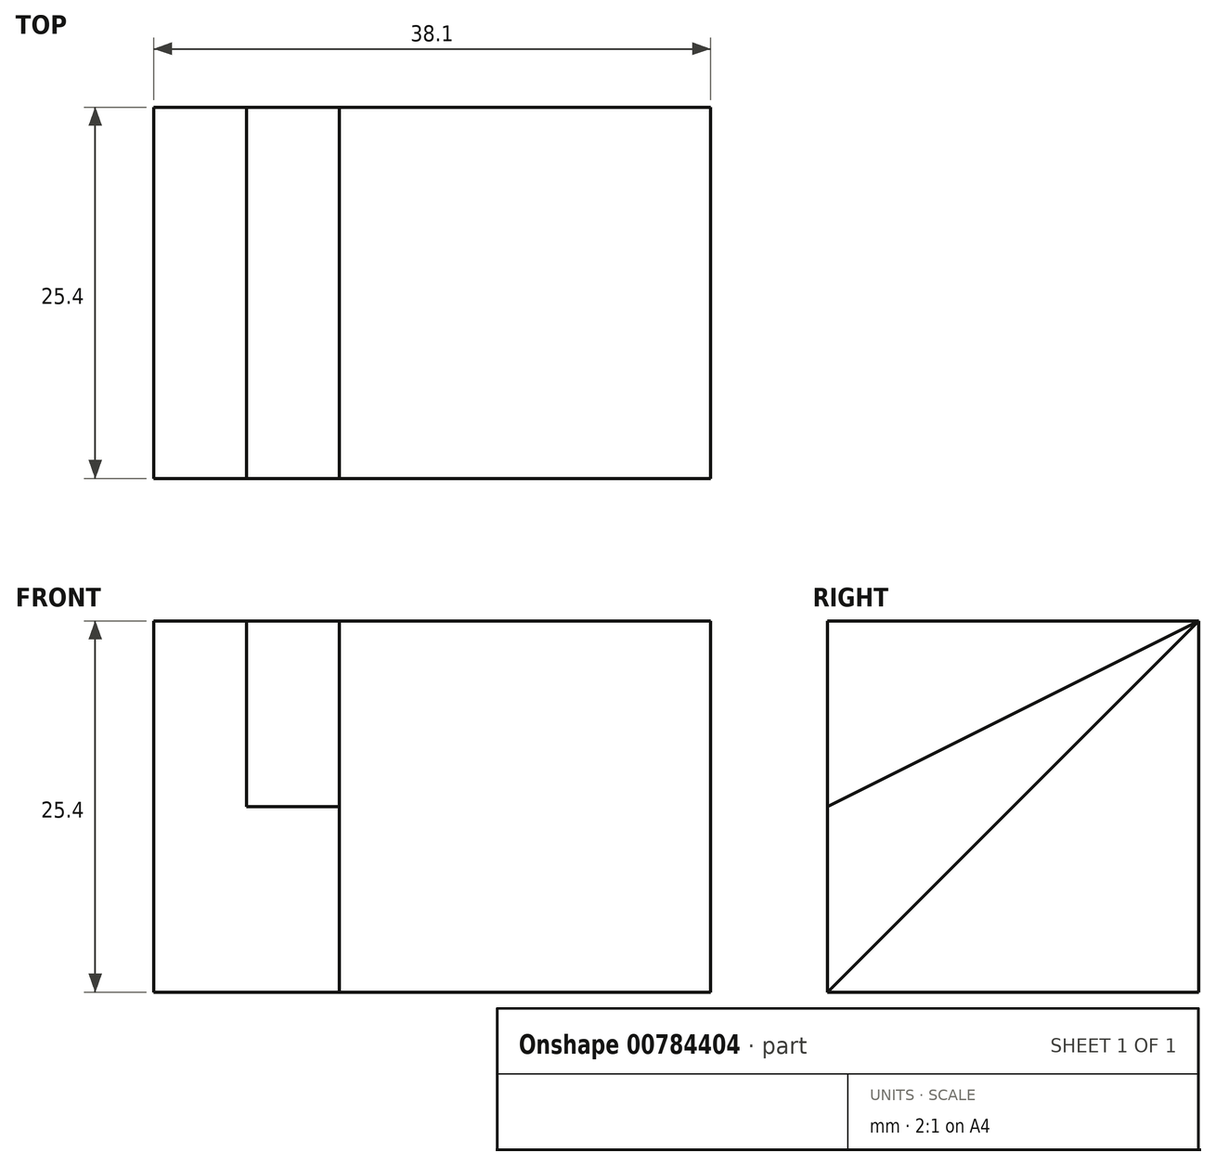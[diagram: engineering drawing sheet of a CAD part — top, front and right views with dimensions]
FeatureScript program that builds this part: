
annotation { "Feature Type Name" : "Feature", "Feature Type Description" : "" }
export const myFeature = defineFeature(function(context is Context, id is Id, definition is map)
    precondition{}
    {
        {
            var Q0;
            Q0=qCreatedBy(makeId("Front.planeOp"),FACE);
            var sketch = newSketch(context, id + "F0", { "sketchPlane" : qUnion([Q0])});
            skLineSegment(sketch, "E0", {"start": v(0, 0) * mm, "end": v(38.1, 0) * mm});
            skLineSegment(sketch, "E1", {"start": v(38.1, 0) * mm, "end": v(38.1, 25.4) * mm});
            skLineSegment(sketch, "E2", {"start": v(38.1, 25.4) * mm, "end": v(0, 25.4) * mm});
            skLineSegment(sketch, "E3", {"start": v(0, 25.4) * mm, "end": v(0, 0) * mm});
            skSolve(sketch);
        }
        {
            var Q0;
            Q0=makeQuery(id+"F0.imprint","IMPRINT",FACE,{"disambiguationData":[TD([[makeQuery(id+"F0.imprint","IMPRINT",EDGE,{"derivedFrom":sQuery(id+"F0.wireOp",EDGE,"E0")}),1.0]])]});
            extrude(context, id + "F1", {"entities" : qUnion([Q0]), "depth" : 25.4 * mm, "offsetDistance" : 25.4 * mm});
        }
        {
            var Q0;
            Q0=makeQuery(id+"F1.opExtrude","SWEPT_FACE",FACE,{"disambiguationData":[OSD([sQuery(id+"F0.wireOp",EDGE,"E1")])]});
            var sketch = newSketch(context, id + "F2", { "sketchPlane" : qUnion([Q0])});
            skLineSegment(sketch, "E4", {"start": v(0, 25.4) * mm, "end": v(-25.4, 0) * mm});
            skSolve(sketch);
        }
        {
            var Q0;
            Q0=makeQuery(id+"F2.imprint","IMPRINT",FACE,{"disambiguationData":[TD([[makeQuery(id+"F2.imprint","IMPRINT",EDGE,{"derivedFrom":sQuery(id+"F2.wireOp",EDGE,"E4")}),-1.0]])]});
            extrude(context, id + "F3", {"entities" : qUnion([Q0]), "operationType" : NewBodyOperationType.REMOVE, "oppositeDirection" : true, "depth" : 25.4 * mm, "offsetDistance" : 25.4 * mm});
        }
        {
            var Q0;
            Q0=makeQuery(id+"F3.boolean.opBoolean","COPY",FACE,{"derivedFrom":makeQuery(id+"F3.opExtrude","CAP_FACE",FACE,{"disambiguationData":[OSD([sQuery(id+"F0.wireOp",EDGE,"E1"),sQuery(id+"F0.wireOp",EDGE,"E2"),sQuery(id+"F2.wireOp",EDGE,"E4")])],"isStart":false})});
            var sketch = newSketch(context, id + "F4", { "sketchPlane" : qUnion([Q0])});
            skLineSegment(sketch, "E5", {"start": v(-25.4, 25.4) * mm, "end": v(-25.4, 12.7) * mm});
            skLineSegment(sketch, "E6", {"start": v(-25.4, 12.7) * mm, "end": v(0, 25.4) * mm});
            skSolve(sketch);
        }
        {
            var Q0;
            Q0=makeQuery(id+"F4.imprint","IMPRINT",FACE,{"disambiguationData":[TD([[makeQuery(id+"F4.imprint","IMPRINT",EDGE,{"derivedFrom":sQuery(id+"F4.wireOp",EDGE,"E5")}),-1.0]])]});
            extrude(context, id + "F5", {"entities" : qUnion([Q0]), "operationType" : NewBodyOperationType.REMOVE, "oppositeDirection" : true, "depth" : 6.35 * mm, "offsetDistance" : 25.4 * mm});
        }
    });
